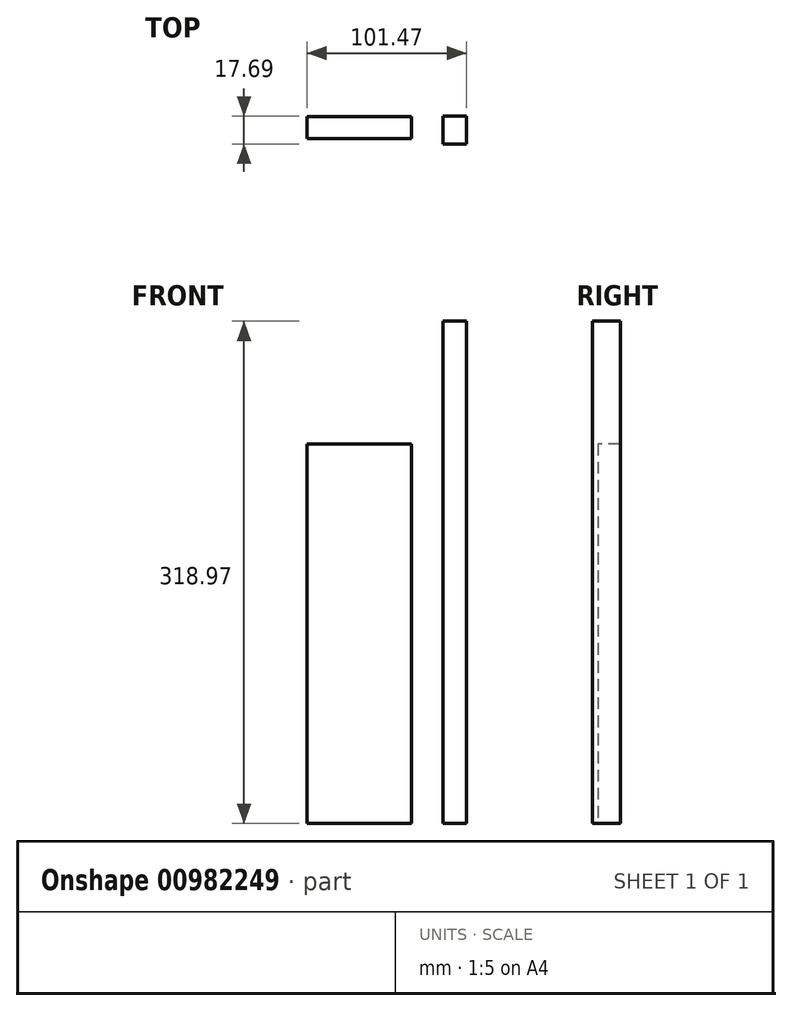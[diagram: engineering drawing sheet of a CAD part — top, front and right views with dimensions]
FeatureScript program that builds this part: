
annotation { "Feature Type Name" : "Feature", "Feature Type Description" : "" }
export const myFeature = defineFeature(function(context is Context, id is Id, definition is map)
    precondition{}
    {
        {
            var Q0;
            Q0=qCreatedBy(makeId("Top.planeOp"),FACE);
            var sketch = newSketch(context, id + "F0", { "sketchPlane" : qUnion([Q0])});
            skLineSegment(sketch, "E0.bottom", {"start": v(-37.52, 0) * mm, "end": v(28.98, 0) * mm});
            skLineSegment(sketch, "E0.top", {"start": v(-37.52, -14.08) * mm, "end": v(28.98, -14.08) * mm});
            skLineSegment(sketch, "E0.left", {"start": v(-37.52, 0) * mm, "end": v(-37.52, -14.08) * mm});
            skLineSegment(sketch, "E0.right", {"start": v(28.98, 0) * mm, "end": v(28.98, -14.08) * mm});
            skSolve(sketch);
        }
        {
            var Q0;
            Q0 = qSketchRegion(id + "F0", true);
            extrude(context, id + "F1", {"entities" : qUnion([Q0]), "depth" : 241.06 * mm, "offsetDistance" : 25.4 * mm});
        }
        {
            var Q0;
            Q0=qCreatedBy(makeId("Top.planeOp"),FACE);
            var sketch = newSketch(context, id + "F2", { "sketchPlane" : qUnion([Q0])});
            skLineSegment(sketch, "E1.bottom", {"start": v(63.95, -17.56) * mm, "end": v(48.9, -17.56) * mm});
            skLineSegment(sketch, "E1.top", {"start": v(63.95, 0.13) * mm, "end": v(48.9, 0.13) * mm});
            skLineSegment(sketch, "E1.left", {"start": v(63.95, -17.56) * mm, "end": v(63.95, 0.13) * mm});
            skLineSegment(sketch, "E1.right", {"start": v(48.9, -17.56) * mm, "end": v(48.9, 0.13) * mm});
            skPoint(sketch, "E1.middle", {"position": v(56.43, -8.71) * mm});
            skSolve(sketch);
        }
        {
            var Q0;
            Q0 = qSketchRegion(id + "F2", true);
            extrude(context, id + "F3", {"entities" : qUnion([Q0]), "depth" : 318.97 * mm, "offsetDistance" : 25.4 * mm});
        }
    });
